# Revit family: Columns_&_Screens-Teknion-RPSLG_One_Inch_Floor_Screen_With_Glass_Lateral_Connection-R2019
name_source: partatom
category: Furniture
units: mm (PartAtom-declared; Revit-internal decimal feet)

## family parameters
Always vertical = Yes
Cut with Voids When Loaded = No
OmniClass Number = 23.40.20.00
OmniClass Title = General Furniture and Specialties
Room Calculation Point = No
Shared = Yes
Work Plane-Based = No

## types (6) — shared parameters
Assembly Code = E2020200
Manufacturer = Teknion
Manufacturer Fax = 416.661.4586
Part Number = RPSLG
Product Documentation Link = https://www.teknion.com
Product Line = Expansion Desking
Product Page URL = https://www.teknion.com
Series = Expansion Desking
Sustainability Data = https://www.teknion.com
URL = www.teknion.com
Unit Weight URL = http://www.teknion.com
Warranty = http://www.teknion.com

## per-type parameters (varying)
| type | Description | Height | Left Configuration | Model | Right Configuration | Shared Configuration |
| 42" Height, Left Configuration | 1" Floor Screen with Glass Lateral Connection, 42" Height, Left Configuration | 42 " | Yes | RPSLG42____L | No | No |
| 42" Height, Right Configuration | 1" Floor Screen with Glass Lateral Connection, 42" Height, Right Configuration | 42 " | No | RPSLG42____R | Yes | No |
| 42" Height, Shared Configuration | 1" Floor Screen with Glass Lateral Connection, 42" Height, Shared Configuration | 42 " | No | RPSLG42____S | No | Yes |
| 51" Height, Left Configuration | 1" Floor Screen with Glass Lateral Connection, 51" Height, Left Configuration | 50.831 " | Yes | RPSLG51____L | No | No |
| 51" Height, Right Configuration | 1" Floor Screen with Glass Lateral Connection, 51" Height, Right Configuration | 50.831 " | No | RPSLG51____R | Yes | No |
| 51" Height, Shared Configuration | 1" Floor Screen with Glass Lateral Connection, 51" Height, Shared Configuration | 50.831 " | No | RPSLG51____S | No | Yes |

## geometry (parser evidence)
native form markers: Sweep x2
no freeform markers — native parametric forms only
